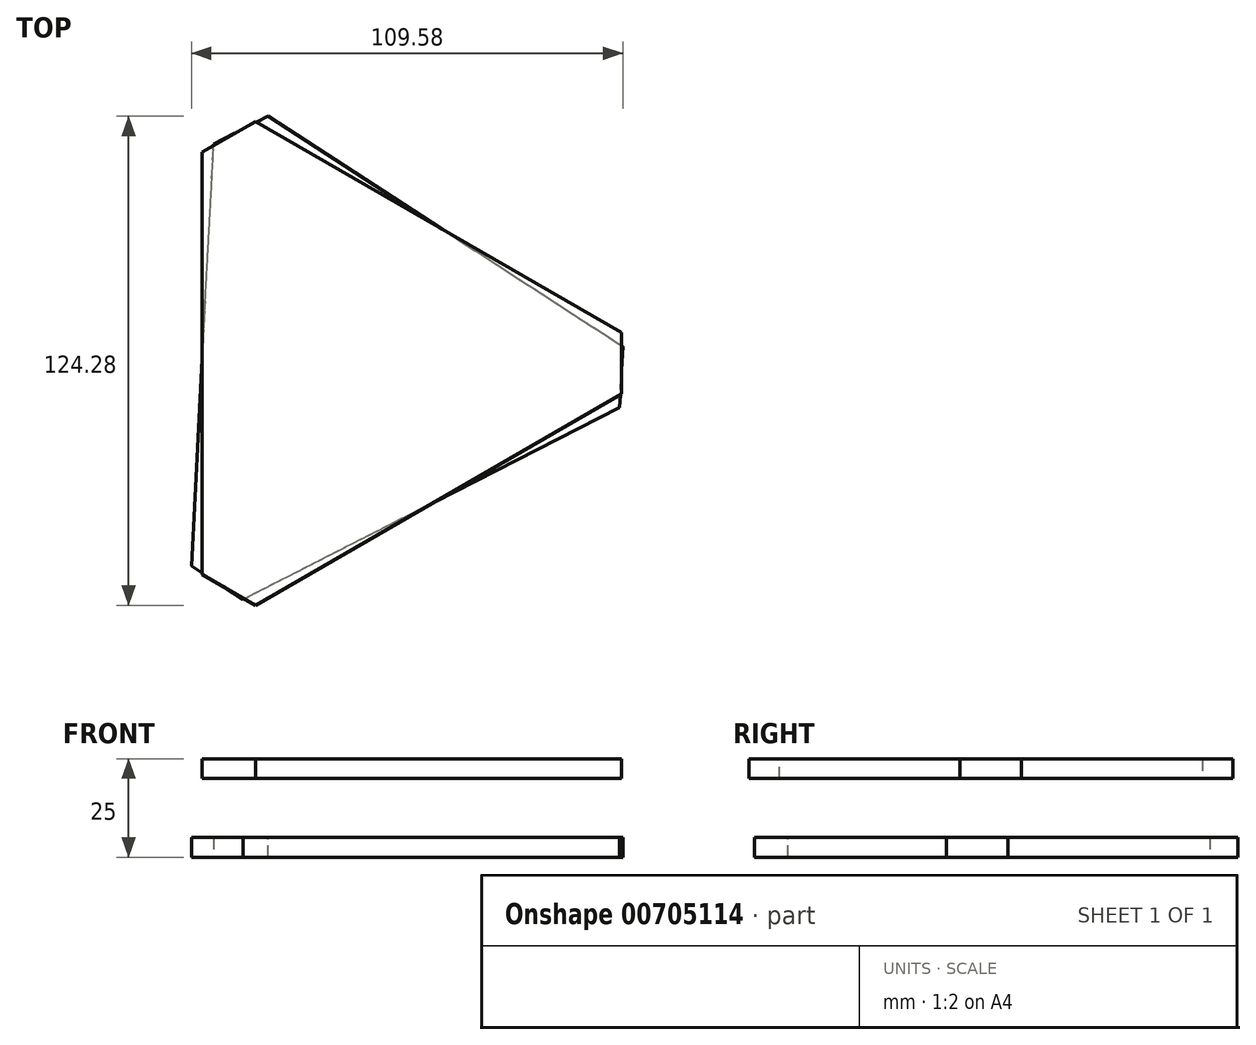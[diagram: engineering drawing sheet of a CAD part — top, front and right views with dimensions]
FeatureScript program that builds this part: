
annotation { "Feature Type Name" : "Feature", "Feature Type Description" : "" }
export const myFeature = defineFeature(function(context is Context, id is Id, definition is map)
    precondition{}
    {
        {
            var Q0;
            Q0=qCreatedBy(makeId("Top.planeOp"),FACE);
            var sketch = newSketch(context, id + "F0", { "sketchPlane" : qUnion([Q0])});
            skCircle(sketch, "E0.cCircle", {"center": v(0, 0) * mm, "radius": 80 * mm, "construction": true});
            skLineSegment(sketch, "E0.0", {"start": v(80, 0) * mm, "end": v(-40, -69.28) * mm});
            skLineSegment(sketch, "E0.1", {"start": v(-40, -69.28) * mm, "end": v(-40, 69.28) * mm});
            skLineSegment(sketch, "E0.2", {"start": v(-40, 69.28) * mm, "end": v(80, 0) * mm});
            skSolve(sketch);
        }
        {
            var Q0;
            Q0=qCreatedBy(makeId("Right.planeOp"),FACE);
            var sketch = newSketch(context, id + "F1", { "sketchPlane" : qUnion([Q0])});
            skLineSegment(sketch, "E1", {"start": v(0, 62.5) * mm, "end": v(0, -23.07) * mm, "construction": true});
            skSolve(sketch);
        }
        {
            var Q0;
            Q0=makeQuery(id+"F0.imprint","IMPRINT",FACE,{"disambiguationData":[TD([[makeQuery(id+"F0.imprint","IMPRINT",EDGE,{"derivedFrom":sQuery(id+"F0.wireOp",EDGE,"E0.0")}),-1.0]])]});
            extrude(context, id + "F2", {"entities" : qUnion([Q0]), "depth" : 5 * mm, "offsetDistance" : 25 * mm});
        }
        {
            var Q0;
            Q0=makeQuery(id+"F2.opExtrude","SWEPT_EDGE",EDGE,{"disambiguationData":[OSD([sQuery(id+"F0.wireOp",EDGE,"E0.0"),sQuery(id+"F0.wireOp",EDGE,"E0.1")])]});
            var Q1;
            Q1=makeQuery(id+"F2.opExtrude","SWEPT_EDGE",EDGE,{"disambiguationData":[OSD([sQuery(id+"F0.wireOp",EDGE,"E0.0"),sQuery(id+"F0.wireOp",EDGE,"E0.2")])]});
            var Q2;
            Q2=makeQuery(id+"F2.opExtrude","SWEPT_EDGE",EDGE,{"disambiguationData":[OSD([sQuery(id+"F0.wireOp",EDGE,"E0.1"),sQuery(id+"F0.wireOp",EDGE,"E0.2")])]});
            chamfer(context, id + "F3", {"entities" : qUnion([Q0, Q1, Q2]), "width" : 9 * mm, "tangentPropagation" : true});
        }
        {
            var Q0;
            Q0=makeQuery(id+"F2.opExtrude","SWEPT_BODY",BODY,{"disambiguationData":[OSD([sQuery(id+"F0.wireOp",EDGE,"E0.0"),sQuery(id+"F0.wireOp",EDGE,"E0.1"),sQuery(id+"F0.wireOp",EDGE,"E0.2")])]});
            transform(context, id + "F4", {"entities" : qUnion([Q0]), "transformType" : TransformType.TRANSLATION_3D, "dx" : 0 * mm, "dy" : 0 * mm, "dz" : 20 * mm, "makeCopy" : true});
        }
        {
            var Q0;
            Q0=makeQuery(id+"F2.opExtrude","SWEPT_BODY",BODY,{"disambiguationData":[OSD([sQuery(id+"F0.wireOp",EDGE,"E0.0"),sQuery(id+"F0.wireOp",EDGE,"E0.1"),sQuery(id+"F0.wireOp",EDGE,"E0.2")])]});
            var Q1;
            Q1=sQuery(id+"F1.wireOp",EDGE,"E1");
            transform(context, id + "F5", {"entities" : qUnion([Q0]), "transformType" : TransformType.ROTATION, "transformAxis" : qUnion([Q1]), "angle" : 3 * degree, "makeCopy" : false});
        }
    });
